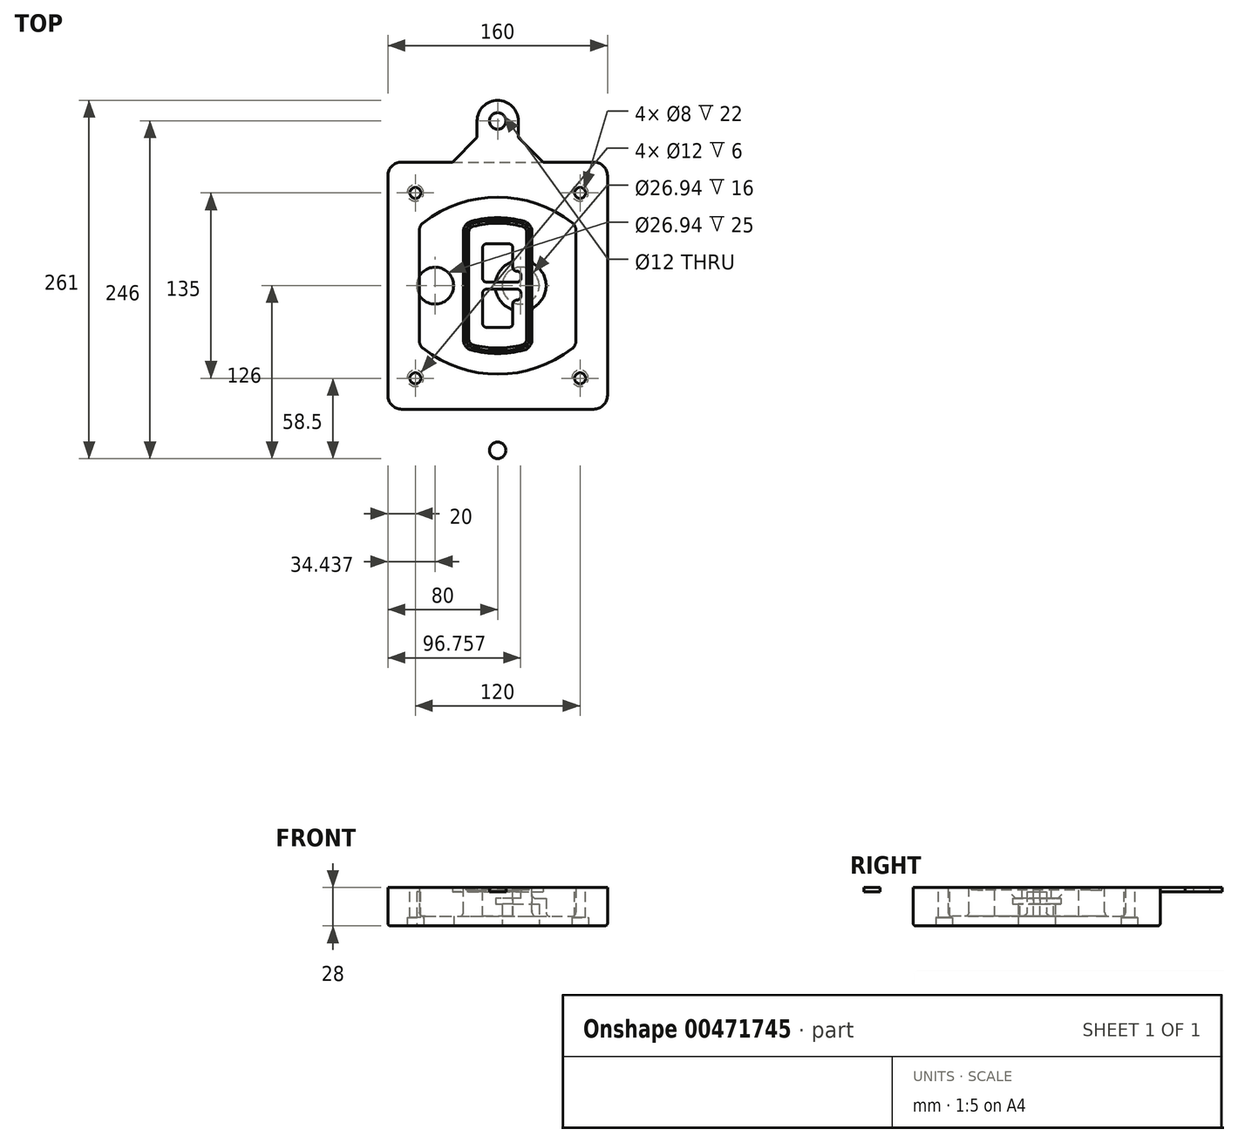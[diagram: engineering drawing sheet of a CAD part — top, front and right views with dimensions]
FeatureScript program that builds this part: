
annotation { "Feature Type Name" : "Feature", "Feature Type Description" : "" }
export const myFeature = defineFeature(function(context is Context, id is Id, definition is map)
    precondition{}
    {
        {
            var Q0;
            Q0=qCreatedBy(makeId("Top.planeOp"),FACE);
            var sketch = newSketch(context, id + "F0", { "sketchPlane" : qUnion([Q0])});
            skPoint(sketch, "E0.rect.middle", {"position": v(0, 0) * mm});
            skLineSegment(sketch, "E1.bottom", {"start": v(-70, -90) * mm, "end": v(70, -90) * mm});
            skLineSegment(sketch, "E1.top", {"start": v(-70, 90) * mm, "end": v(70, 90) * mm});
            skLineSegment(sketch, "E1.left", {"start": v(-80, -80) * mm, "end": v(-80, 80) * mm});
            skLineSegment(sketch, "E1.right", {"start": v(80, -80) * mm, "end": v(80, 80) * mm});
            skLineSegment(sketch, "E2", {"start": v(-80, 90) * mm, "end": v(80, -90) * mm, "construction": true});
            skLineSegment(sketch, "E3", {"start": v(80, 90) * mm, "end": v(-80, -90) * mm, "construction": true});
            skCircle(sketch, "E4", {"center": v(-60, 67.5) * mm, "radius": 4 * mm});
            skCircle(sketch, "E5", {"center": v(60, 67.5) * mm, "radius": 4 * mm});
            skCircle(sketch, "E6", {"center": v(60, -67.5) * mm, "radius": 4 * mm});
            skCircle(sketch, "E7", {"center": v(-60, -67.5) * mm, "radius": 4 * mm});
            skLineSegment(sketch, "E8", {"start": v(-60, 67.5) * mm, "end": v(60, 67.5) * mm, "construction": true});
            skLineSegment(sketch, "E9", {"start": v(60, 67.5) * mm, "end": v(60, -67.5) * mm, "construction": true});
            skLineSegment(sketch, "E10", {"start": v(60, -67.5) * mm, "end": v(-60, -67.5) * mm, "construction": true});
            skLineSegment(sketch, "E11", {"start": v(-60, -67.5) * mm, "end": v(-60, 67.5) * mm, "construction": true});
            skLineSegment(sketch, "E12", {"start": v(-60, 40.3) * mm, "end": v(-60, -40.3) * mm});
            skLineSegment(sketch, "E13", {"start": v(60, 40.3) * mm, "end": v(60, -40.3) * mm});
            skArc(sketch, "E14", {"start": v(56.15, 48.18) * mm, "mid": v(0, 67.5) * mm, "end": v(-56.15, 48.18) * mm});
            skArc(sketch, "E15", {"start": v(-56.15, -48.18) * mm, "mid": v(0, -67.5) * mm, "end": v(56.15, -48.18) * mm});
            skLineSegment(sketch, "E16", {"start": v(-60, 0) * mm, "end": v(60, 0) * mm, "construction": true});
            skPoint(sketch, "E17.visualSharp", {"position": v(-60, -45) * mm});
            skArc(sketch, "E17.filletArc", {"start": v(-60, -40.3) * mm, "mid": v(-58.99, -44.68) * mm, "end": v(-56.15, -48.18) * mm});
            skPoint(sketch, "E18.visualSharp", {"position": v(-60, 45) * mm});
            skArc(sketch, "E18.filletArc", {"start": v(-56.15, 48.18) * mm, "mid": v(-58.99, 44.68) * mm, "end": v(-60, 40.3) * mm});
            skPoint(sketch, "E19.visualSharp", {"position": v(60, 45) * mm});
            skArc(sketch, "E19.filletArc", {"start": v(60, 40.3) * mm, "mid": v(58.99, 44.68) * mm, "end": v(56.15, 48.18) * mm});
            skPoint(sketch, "E20.visualSharp", {"position": v(60, -45) * mm});
            skArc(sketch, "E20.filletArc", {"start": v(56.15, -48.18) * mm, "mid": v(58.99, -44.68) * mm, "end": v(60, -40.3) * mm});
            skPoint(sketch, "E21.visualSharp", {"position": v(-80, 90) * mm});
            skArc(sketch, "E21.filletArc", {"start": v(-70, 90) * mm, "mid": v(-77.07, 87.07) * mm, "end": v(-80, 80) * mm});
            skPoint(sketch, "E22.visualSharp", {"position": v(80, 90) * mm});
            skArc(sketch, "E22.filletArc", {"start": v(80, 80) * mm, "mid": v(77.07, 87.07) * mm, "end": v(70, 90) * mm});
            skPoint(sketch, "E23.visualSharp", {"position": v(80, -90) * mm});
            skArc(sketch, "E23.filletArc", {"start": v(70, -90) * mm, "mid": v(77.07, -87.07) * mm, "end": v(80, -80) * mm});
            skPoint(sketch, "E24.visualSharp", {"position": v(-80, -90) * mm});
            skArc(sketch, "E24.filletArc", {"start": v(-80, -80) * mm, "mid": v(-77.07, -87.07) * mm, "end": v(-70, -90) * mm});
            skArc(sketch, "E25.0", {"start": v(57, 40.3) * mm, "mid": v(56.3, 43.36) * mm, "end": v(54.3, 45.81) * mm});
            skLineSegment(sketch, "E25.1", {"start": v(57, 40.3) * mm, "end": v(57, -40.3) * mm});
            skArc(sketch, "E25.2", {"start": v(54.3, -45.81) * mm, "mid": v(56.3, -43.36) * mm, "end": v(57, -40.3) * mm});
            skArc(sketch, "E25.3", {"start": v(-54.3, -45.81) * mm, "mid": v(0, -64.5) * mm, "end": v(54.3, -45.81) * mm});
            skArc(sketch, "E25.4", {"start": v(-57, -40.3) * mm, "mid": v(-56.3, -43.36) * mm, "end": v(-54.3, -45.81) * mm});
            skArc(sketch, "E25.5", {"start": v(54.3, 45.81) * mm, "mid": v(0, 64.5) * mm, "end": v(-54.3, 45.81) * mm});
            skLineSegment(sketch, "E25.6", {"start": v(-57, 40.3) * mm, "end": v(-57, -40.3) * mm});
            skArc(sketch, "E25.7", {"start": v(-54.3, 45.81) * mm, "mid": v(-56.3, 43.36) * mm, "end": v(-57, 40.3) * mm});
            skArc(sketch, "E26.0", {"start": v(-58.62, 51.33) * mm, "mid": v(-62.58, 46.43) * mm, "end": v(-64, 40.3) * mm});
            skArc(sketch, "E26.1", {"start": v(58.62, 51.33) * mm, "mid": v(0, 71.5) * mm, "end": v(-58.62, 51.33) * mm});
            skArc(sketch, "E26.2", {"start": v(64, 40.3) * mm, "mid": v(62.58, 46.43) * mm, "end": v(58.62, 51.33) * mm});
            skLineSegment(sketch, "E26.3", {"start": v(64, 40.3) * mm, "end": v(64, -40.3) * mm});
            skArc(sketch, "E26.4", {"start": v(58.62, -51.33) * mm, "mid": v(62.58, -46.43) * mm, "end": v(64, -40.3) * mm});
            skLineSegment(sketch, "E26.5", {"start": v(-64, 40.3) * mm, "end": v(-64, -40.3) * mm});
            skArc(sketch, "E26.6", {"start": v(-58.62, -51.33) * mm, "mid": v(0, -71.5) * mm, "end": v(58.62, -51.33) * mm});
            skArc(sketch, "E26.7", {"start": v(-64, -40.3) * mm, "mid": v(-62.58, -46.43) * mm, "end": v(-58.62, -51.33) * mm});
            skSolve(sketch);
        }
        {
            var Q0;
            Q0=makeQuery(id+"F0.imprint","IMPRINT",FACE,{"disambiguationData":[TD([[makeQuery(id+"F0.imprint","IMPRINT",EDGE,{"derivedFrom":sQuery(id+"F0.wireOp",EDGE,"E1.bottom")}),1.0]])]});
            var Q1;
            Q1=makeQuery(id+"F0.imprint","IMPRINT",FACE,{"disambiguationData":[TD([[makeQuery(id+"F0.imprint","IMPRINT",EDGE,{"derivedFrom":sQuery(id+"F0.wireOp",EDGE,"E12")}),1.0]])]});
            var Q2;
            Q2=makeQuery(id+"F0.imprint","IMPRINT",FACE,{"disambiguationData":[TD([[makeQuery(id+"F0.imprint","IMPRINT",EDGE,{"derivedFrom":sQuery(id+"F0.wireOp",EDGE,"E25.0")}),1.0]])]});
            var Q3;
            Q3=makeQuery(id+"F0.imprint","IMPRINT",FACE,{"disambiguationData":[TD([[makeQuery(id+"F0.imprint","IMPRINT",EDGE,{"derivedFrom":sQuery(id+"F0.wireOp",EDGE,"E12")}),-1.0]])]});
            extrude(context, id + "F1", {"entities" : qUnion([Q0, Q1, Q2, Q3]), "oppositeDirection" : true, "depth" : 25 * mm});
        }
        {
            var Q0;
            Q0=makeQuery(id+"F0.imprint","IMPRINT",FACE,{"disambiguationData":[TD([[makeQuery(id+"F0.imprint","IMPRINT",EDGE,{"derivedFrom":sQuery(id+"F0.wireOp",EDGE,"E12")}),1.0]])]});
            extrude(context, id + "F2", {"entities" : qUnion([Q0]), "operationType" : NewBodyOperationType.ADD, "depth" : 3 * mm});
        }
        {
            var Q0;
            Q0=makeQuery(id+"F0.imprint","IMPRINT",FACE,{"disambiguationData":[TD([[makeQuery(id+"F0.imprint","IMPRINT",EDGE,{"derivedFrom":sQuery(id+"F0.wireOp",EDGE,"E25.0")}),1.0]])]});
            extrude(context, id + "F3", {"entities" : qUnion([Q0]), "operationType" : NewBodyOperationType.REMOVE, "oppositeDirection" : true, "depth" : 18 * mm});
        }
        {
            var Q0;
            Q0=makeQuery(id+"F2.opExtrude","CAP_FACE",FACE,{"disambiguationData":[OSD([sQuery(id+"F0.wireOp",EDGE,"E12"),sQuery(id+"F0.wireOp",EDGE,"E13"),sQuery(id+"F0.wireOp",EDGE,"E14"),sQuery(id+"F0.wireOp",EDGE,"E15"),sQuery(id+"F0.wireOp",EDGE,"E17.filletArc"),sQuery(id+"F0.wireOp",EDGE,"E18.filletArc"),sQuery(id+"F0.wireOp",EDGE,"E19.filletArc"),sQuery(id+"F0.wireOp",EDGE,"E20.filletArc"),sQuery(id+"F0.wireOp",EDGE,"E25.0"),sQuery(id+"F0.wireOp",EDGE,"E25.1"),sQuery(id+"F0.wireOp",EDGE,"E25.2"),sQuery(id+"F0.wireOp",EDGE,"E25.3"),sQuery(id+"F0.wireOp",EDGE,"E25.4"),sQuery(id+"F0.wireOp",EDGE,"E25.5"),sQuery(id+"F0.wireOp",EDGE,"E25.6"),sQuery(id+"F0.wireOp",EDGE,"E25.7")])],"isStart":false});
            var sketch = newSketch(context, id + "F4", { "sketchPlane" : qUnion([Q0])});
            skArc(sketch, "E27.0", {"start": v(-19.08, -46.97) * mm, "mid": v(0, -49.5) * mm, "end": v(19.08, -46.97) * mm});
            skArc(sketch, "E28.0", {"start": v(19.08, 46.97) * mm, "mid": v(0, 49.5) * mm, "end": v(-19.08, 46.97) * mm});
            skLineSegment(sketch, "E29", {"start": v(-25, 39.25) * mm, "end": v(-25, -39.25) * mm});
            skLineSegment(sketch, "E30", {"start": v(25, 39.25) * mm, "end": v(25, -39.25) * mm});
            skLineSegment(sketch, "E31", {"start": v(-25, 45.1) * mm, "end": v(25, 45.1) * mm, "construction": true});
            skLineSegment(sketch, "E32", {"start": v(-25, -45.1) * mm, "end": v(25, -45.1) * mm, "construction": true});
            skPoint(sketch, "E33.visualSharp", {"position": v(-25, 45.1) * mm});
            skArc(sketch, "E33.filletArc", {"start": v(-19.08, 46.97) * mm, "mid": v(-23.35, 44.11) * mm, "end": v(-25, 39.25) * mm});
            skPoint(sketch, "E34.visualSharp", {"position": v(25, 45.1) * mm});
            skArc(sketch, "E34.filletArc", {"start": v(25, 39.25) * mm, "mid": v(23.35, 44.11) * mm, "end": v(19.08, 46.97) * mm});
            skPoint(sketch, "E35.visualSharp", {"position": v(25, -45.1) * mm});
            skArc(sketch, "E35.filletArc", {"start": v(19.08, -46.97) * mm, "mid": v(23.35, -44.11) * mm, "end": v(25, -39.25) * mm});
            skPoint(sketch, "E36.visualSharp", {"position": v(-25, -45.1) * mm});
            skArc(sketch, "E36.filletArc", {"start": v(-25, -39.25) * mm, "mid": v(-23.35, -44.11) * mm, "end": v(-19.08, -46.97) * mm});
            skArc(sketch, "E37.0", {"start": v(54.3, 45.81) * mm, "mid": v(0, 64.5) * mm, "end": v(-54.3, 45.81) * mm});
            skArc(sketch, "E37.1", {"start": v(-54.3, 45.81) * mm, "mid": v(-56.3, 43.36) * mm, "end": v(-57, 40.3) * mm});
            skLineSegment(sketch, "E37.2", {"start": v(-57, 40.3) * mm, "end": v(-57, -40.3) * mm});
            skArc(sketch, "E37.3", {"start": v(-57, -40.3) * mm, "mid": v(-56.3, -43.36) * mm, "end": v(-54.3, -45.81) * mm});
            skArc(sketch, "E37.4", {"start": v(-54.3, -45.81) * mm, "mid": v(0, -64.5) * mm, "end": v(54.3, -45.81) * mm});
            skArc(sketch, "E37.5", {"start": v(54.3, -45.81) * mm, "mid": v(56.3, -43.36) * mm, "end": v(57, -40.3) * mm});
            skLineSegment(sketch, "E37.6", {"start": v(57, 40.3) * mm, "end": v(57, -40.3) * mm});
            skArc(sketch, "E37.7", {"start": v(57, 40.3) * mm, "mid": v(56.3, 43.36) * mm, "end": v(54.3, 45.81) * mm});
            skLineSegment(sketch, "E38.0", {"start": v(23, 39.25) * mm, "end": v(23, -39.25) * mm});
            skArc(sketch, "E38.1", {"start": v(18.56, -45.04) * mm, "mid": v(21.76, -42.9) * mm, "end": v(23, -39.25) * mm});
            skArc(sketch, "E38.2", {"start": v(-18.56, -45.04) * mm, "mid": v(0, -47.5) * mm, "end": v(18.56, -45.04) * mm});
            skArc(sketch, "E38.3", {"start": v(-23, -39.25) * mm, "mid": v(-21.76, -42.9) * mm, "end": v(-18.56, -45.04) * mm});
            skLineSegment(sketch, "E38.4", {"start": v(-23, 39.25) * mm, "end": v(-23, -39.25) * mm});
            skArc(sketch, "E38.5", {"start": v(23, 39.25) * mm, "mid": v(21.76, 42.9) * mm, "end": v(18.56, 45.04) * mm});
            skArc(sketch, "E38.6", {"start": v(-18.56, 45.04) * mm, "mid": v(-21.76, 42.9) * mm, "end": v(-23, 39.25) * mm});
            skArc(sketch, "E38.7", {"start": v(18.56, 45.04) * mm, "mid": v(0, 47.5) * mm, "end": v(-18.56, 45.04) * mm});
            skArc(sketch, "E39.0", {"start": v(21, 39.25) * mm, "mid": v(20.18, 41.68) * mm, "end": v(18.04, 43.1) * mm});
            skLineSegment(sketch, "E39.1", {"start": v(21, 39.25) * mm, "end": v(21, -39.25) * mm});
            skArc(sketch, "E39.2", {"start": v(18.04, -43.1) * mm, "mid": v(20.18, -41.68) * mm, "end": v(21, -39.25) * mm});
            skArc(sketch, "E39.3", {"start": v(-18.04, -43.1) * mm, "mid": v(0, -45.5) * mm, "end": v(18.04, -43.1) * mm});
            skArc(sketch, "E39.4", {"start": v(-21, -39.25) * mm, "mid": v(-20.18, -41.68) * mm, "end": v(-18.04, -43.1) * mm});
            skArc(sketch, "E39.5", {"start": v(18.04, 43.1) * mm, "mid": v(0, 45.5) * mm, "end": v(-18.04, 43.1) * mm});
            skLineSegment(sketch, "E39.6", {"start": v(-21, 39.25) * mm, "end": v(-21, -39.25) * mm});
            skArc(sketch, "E39.7", {"start": v(-18.04, 43.1) * mm, "mid": v(-20.18, 41.68) * mm, "end": v(-21, 39.25) * mm});
            skLineSegment(sketch, "E40", {"start": v(-25, 0) * mm, "end": v(25, 0) * mm, "construction": true});
            skLineSegment(sketch, "E41", {"start": v(-11, 5.5) * mm, "end": v(-11, 27.5) * mm});
            skLineSegment(sketch, "E42", {"start": v(-8, 30.5) * mm, "end": v(8, 30.5) * mm});
            skLineSegment(sketch, "E43", {"start": v(11, 27.5) * mm, "end": v(11, 13.5) * mm});
            skLineSegment(sketch, "E44", {"start": v(14, 10.5) * mm, "end": v(14, 10.5) * mm});
            skLineSegment(sketch, "E45", {"start": v(17, 7.5) * mm, "end": v(17, 5.5) * mm});
            skLineSegment(sketch, "E46", {"start": v(14, 2.5) * mm, "end": v(-8, 2.5) * mm});
            skPoint(sketch, "E47.visualSharp", {"position": v(-11, 30.5) * mm});
            skArc(sketch, "E47.filletArc", {"start": v(-8, 30.5) * mm, "mid": v(-10.12, 29.62) * mm, "end": v(-11, 27.5) * mm});
            skPoint(sketch, "E48.visualSharp", {"position": v(11, 30.5) * mm});
            skArc(sketch, "E48.filletArc", {"start": v(11, 27.5) * mm, "mid": v(10.12, 29.62) * mm, "end": v(8, 30.5) * mm});
            skPoint(sketch, "E49.visualSharp", {"position": v(11, 10.5) * mm});
            skArc(sketch, "E49.filletArc", {"start": v(11, 13.5) * mm, "mid": v(11.88, 11.38) * mm, "end": v(14, 10.5) * mm});
            skPoint(sketch, "E50.visualSharp", {"position": v(17, 10.5) * mm});
            skArc(sketch, "E50.filletArc", {"start": v(17, 7.5) * mm, "mid": v(16.12, 9.62) * mm, "end": v(14, 10.5) * mm});
            skPoint(sketch, "E51.visualSharp", {"position": v(17, 2.5) * mm});
            skArc(sketch, "E51.filletArc", {"start": v(14, 2.5) * mm, "mid": v(16.12, 3.38) * mm, "end": v(17, 5.5) * mm});
            skPoint(sketch, "E52.visualSharp", {"position": v(-11, 2.5) * mm});
            skArc(sketch, "E52.filletArc", {"start": v(-11, 5.5) * mm, "mid": v(-10.12, 3.38) * mm, "end": v(-8, 2.5) * mm});
            skLineSegment(sketch, "E53.0.MirrorCS", {"start": v(14, -2.5) * mm, "end": v(-8, -2.5) * mm});
            skArc(sketch, "E54.0.MirrorCS", {"start": v(-11, -5.5) * mm, "mid": v(-10.12, -3.38) * mm, "end": v(-8, -2.5) * mm});
            skLineSegment(sketch, "E55.0.MirrorCS", {"start": v(-11, -5.5) * mm, "end": v(-11, -27.5) * mm});
            skArc(sketch, "E56.0.MirrorCS", {"start": v(-8, -30.5) * mm, "mid": v(-10.12, -29.62) * mm, "end": v(-11, -27.5) * mm});
            skLineSegment(sketch, "E57.0.MirrorCS", {"start": v(-8, -30.5) * mm, "end": v(8, -30.5) * mm});
            skArc(sketch, "E58.0.MirrorCS", {"start": v(11, -27.5) * mm, "mid": v(10.12, -29.62) * mm, "end": v(8, -30.5) * mm});
            skLineSegment(sketch, "E59.0.MirrorCS", {"start": v(11, -27.5) * mm, "end": v(11, -13.5) * mm});
            skArc(sketch, "E60.0.MirrorCS", {"start": v(11, -13.5) * mm, "mid": v(11.88, -11.38) * mm, "end": v(14, -10.5) * mm});
            skArc(sketch, "E61.0.MirrorCS", {"start": v(17, -7.5) * mm, "mid": v(16.12, -9.62) * mm, "end": v(14, -10.5) * mm});
            skLineSegment(sketch, "E62.0.MirrorCS", {"start": v(17, -7.5) * mm, "end": v(17, -5.5) * mm});
            skArc(sketch, "E63.0.MirrorCS", {"start": v(14, -2.5) * mm, "mid": v(16.12, -3.38) * mm, "end": v(17, -5.5) * mm});
            skSolve(sketch);
        }
        {
            var Q0;
            Q0=makeQuery(id+"F4.imprint","IMPRINT",FACE,{"disambiguationData":[TD([[makeQuery(id+"F4.imprint","IMPRINT",EDGE,{"derivedFrom":sQuery(id+"F4.wireOp",EDGE,"E27.0")}),1.0]])]});
            var Q1;
            Q1=makeQuery(id+"F4.imprint","IMPRINT",FACE,{"disambiguationData":[TD([[makeQuery(id+"F4.imprint","IMPRINT",EDGE,{"derivedFrom":sQuery(id+"F4.wireOp",EDGE,"E38.0")}),-1.0]])]});
            var Q2;
            Q2=makeQuery(id+"F4.imprint","IMPRINT",FACE,{"disambiguationData":[TD([[makeQuery(id+"F4.imprint","IMPRINT",EDGE,{"derivedFrom":sQuery(id+"F4.wireOp",EDGE,"E39.0")}),1.0]])]});
            extrude(context, id + "F5", {"entities" : qUnion([Q0, Q1, Q2]), "operationType" : NewBodyOperationType.ADD, "endBound" : BoundingType.UP_TO_NEXT, "oppositeDirection" : true, "depth" : 25 * mm});
        }
        {
            var Q0;
            Q0=makeQuery(id+"F4.imprint","IMPRINT",FACE,{"disambiguationData":[TD([[makeQuery(id+"F4.imprint","IMPRINT",EDGE,{"derivedFrom":sQuery(id+"F4.wireOp",EDGE,"E38.0")}),-1.0]])]});
            extrude(context, id + "F6", {"entities" : qUnion([Q0]), "operationType" : NewBodyOperationType.REMOVE, "oppositeDirection" : true, "depth" : 2 * mm});
        }
        {
            var Q0;
            Q0=makeQuery(id+"F1.opExtrude","CAP_FACE",FACE,{"disambiguationData":[OSD([sQuery(id+"F0.wireOp",EDGE,"E1.bottom"),sQuery(id+"F0.wireOp",EDGE,"E1.top"),sQuery(id+"F0.wireOp",EDGE,"E1.left"),sQuery(id+"F0.wireOp",EDGE,"E1.right"),sQuery(id+"F0.wireOp",EDGE,"E4"),sQuery(id+"F0.wireOp",EDGE,"E5"),sQuery(id+"F0.wireOp",EDGE,"E6"),sQuery(id+"F0.wireOp",EDGE,"E7"),sQuery(id+"F0.wireOp",EDGE,"E21.filletArc"),sQuery(id+"F0.wireOp",EDGE,"E22.filletArc"),sQuery(id+"F0.wireOp",EDGE,"E23.filletArc"),sQuery(id+"F0.wireOp",EDGE,"E24.filletArc")])],"isStart":false});
            var sketch = newSketch(context, id + "F7", { "sketchPlane" : qUnion([Q0])});
            skCircle(sketch, "E64", {"center": v(16.76, 0) * mm, "radius": 13.47 * mm});
            skCircle(sketch, "E65", {"center": v(-45.56, 0) * mm, "radius": 13.47 * mm});
            skLineSegment(sketch, "E66", {"start": v(80, 0) * mm, "end": v(-80, 0) * mm});
            skCircle(sketch, "E67", {"center": v(16.76, 0) * mm, "radius": 18.47 * mm});
            skCircle(sketch, "E68", {"center": v(60, -67.5) * mm, "radius": 6 * mm});
            skCircle(sketch, "E69", {"center": v(-60, -67.5) * mm, "radius": 6 * mm});
            skCircle(sketch, "E70", {"center": v(-60, 67.5) * mm, "radius": 6 * mm});
            skCircle(sketch, "E71", {"center": v(60, 67.5) * mm, "radius": 6 * mm});
            skSolve(sketch);
        }
        {
            var Q0;
            {var subQ1=sQuery(id+"F7.wireOp",EDGE,"E66");var subQ4=sQuery(id+"F7.wireOp",EDGE,"E64");var subQ6=makeQuery(id+"F7.imprint","INTERSECT",VERTEX,{"disambiguationData":[OD(0.0)],"derivedFrom":[subQ4,subQ1]});Q0=makeQuery(id+"F7.imprint","IMPRINT",FACE,{"disambiguationData":[TD([[makeQuery(id+"F7.imprint","IMPRINT",EDGE,{"disambiguationData":[TD([[subQ6,-1.0]])],"derivedFrom":subQ4}),-1.0]])]});}
            var Q1;
            {var subQ0=sQuery(id+"F7.wireOp",EDGE,"E66");var subQ1=sQuery(id+"F7.wireOp",EDGE,"E64");var subQ3=makeQuery(id+"F7.imprint","INTERSECT",VERTEX,{"disambiguationData":[OD(0.0)],"derivedFrom":[subQ1,subQ0]});Q1=makeQuery(id+"F7.imprint","IMPRINT",FACE,{"disambiguationData":[TD([[makeQuery(id+"F7.imprint","IMPRINT",EDGE,{"disambiguationData":[TD([[subQ3,-1.0]])],"derivedFrom":subQ1}),1.0]])]});}
            var Q2;
            {var subQ0=sQuery(id+"F7.wireOp",EDGE,"E66");var subQ1=sQuery(id+"F7.wireOp",EDGE,"E64");var subQ3=makeQuery(id+"F7.imprint","INTERSECT",VERTEX,{"disambiguationData":[OD(0.0)],"derivedFrom":[subQ1,subQ0]});Q2=makeQuery(id+"F7.imprint","IMPRINT",FACE,{"disambiguationData":[TD([[makeQuery(id+"F7.imprint","IMPRINT",EDGE,{"disambiguationData":[TD([[subQ3,1.0]])],"derivedFrom":subQ1}),1.0]])]});}
            var Q3;
            {var subQ1=sQuery(id+"F7.wireOp",EDGE,"E66");var subQ4=sQuery(id+"F7.wireOp",EDGE,"E64");var subQ6=makeQuery(id+"F7.imprint","INTERSECT",VERTEX,{"disambiguationData":[OD(0.0)],"derivedFrom":[subQ4,subQ1]});Q3=makeQuery(id+"F7.imprint","IMPRINT",FACE,{"disambiguationData":[TD([[makeQuery(id+"F7.imprint","IMPRINT",EDGE,{"disambiguationData":[TD([[subQ6,1.0]])],"derivedFrom":subQ4}),-1.0]])]});}
            extrude(context, id + "F8", {"entities" : qUnion([Q0, Q1, Q2, Q3]), "operationType" : NewBodyOperationType.ADD, "oppositeDirection" : true, "depth" : 20 * mm});
        }
        {
            var Q0;
            {var subQ0=sQuery(id+"F7.wireOp",EDGE,"E66");var subQ1=sQuery(id+"F7.wireOp",EDGE,"E64");var subQ3=makeQuery(id+"F7.imprint","INTERSECT",VERTEX,{"disambiguationData":[OD(0.0)],"derivedFrom":[subQ1,subQ0]});Q0=makeQuery(id+"F7.imprint","IMPRINT",FACE,{"disambiguationData":[TD([[makeQuery(id+"F7.imprint","IMPRINT",EDGE,{"disambiguationData":[TD([[subQ3,-1.0]])],"derivedFrom":subQ1}),1.0]])]});}
            var Q1;
            {var subQ0=sQuery(id+"F7.wireOp",EDGE,"E66");var subQ1=sQuery(id+"F7.wireOp",EDGE,"E64");var subQ3=makeQuery(id+"F7.imprint","INTERSECT",VERTEX,{"disambiguationData":[OD(0.0)],"derivedFrom":[subQ1,subQ0]});Q1=makeQuery(id+"F7.imprint","IMPRINT",FACE,{"disambiguationData":[TD([[makeQuery(id+"F7.imprint","IMPRINT",EDGE,{"disambiguationData":[TD([[subQ3,1.0]])],"derivedFrom":subQ1}),1.0]])]});}
            extrude(context, id + "F9", {"entities" : qUnion([Q0, Q1]), "operationType" : NewBodyOperationType.REMOVE, "oppositeDirection" : true, "depth" : 16 * mm});
        }
        {
            var Q0;
            {var subQ0=sQuery(id+"F7.wireOp",EDGE,"E66");var subQ1=sQuery(id+"F7.wireOp",EDGE,"E65");var subQ3=makeQuery(id+"F7.imprint","INTERSECT",VERTEX,{"disambiguationData":[OD(0.0)],"derivedFrom":[subQ1,subQ0]});Q0=makeQuery(id+"F7.imprint","IMPRINT",FACE,{"disambiguationData":[TD([[makeQuery(id+"F7.imprint","IMPRINT",EDGE,{"disambiguationData":[TD([[subQ3,-1.0]])],"derivedFrom":subQ1}),1.0]])]});}
            var Q1;
            {var subQ0=sQuery(id+"F7.wireOp",EDGE,"E66");var subQ1=sQuery(id+"F7.wireOp",EDGE,"E65");var subQ3=makeQuery(id+"F7.imprint","INTERSECT",VERTEX,{"disambiguationData":[OD(0.0)],"derivedFrom":[subQ1,subQ0]});Q1=makeQuery(id+"F7.imprint","IMPRINT",FACE,{"disambiguationData":[TD([[makeQuery(id+"F7.imprint","IMPRINT",EDGE,{"disambiguationData":[TD([[subQ3,1.0]])],"derivedFrom":subQ1}),1.0]])]});}
            extrude(context, id + "F10", {"entities" : qUnion([Q0, Q1]), "operationType" : NewBodyOperationType.REMOVE, "oppositeDirection" : true, "depth" : 25 * mm});
        }
        {
            var Q0;
            Q0=makeQuery(id+"F7.imprint","IMPRINT",FACE,{"disambiguationData":[TD([[makeQuery(id+"F7.imprint","IMPRINT",EDGE,{"derivedFrom":sQuery(id+"F7.wireOp",EDGE,"E68")}),1.0]])]});
            var Q1;
            Q1=makeQuery(id+"F7.imprint","IMPRINT",FACE,{"disambiguationData":[TD([[makeQuery(id+"F7.imprint","IMPRINT",EDGE,{"derivedFrom":makeQuery(id+"F1.opExtrude","CAP_EDGE",EDGE,{"disambiguationData":[OSD([sQuery(id+"F0.wireOp",EDGE,"E5")])],"isStart":false})}),-1.0]])]});
            var Q2;
            Q2=makeQuery(id+"F7.imprint","IMPRINT",FACE,{"disambiguationData":[TD([[makeQuery(id+"F7.imprint","IMPRINT",EDGE,{"derivedFrom":sQuery(id+"F7.wireOp",EDGE,"E69")}),1.0]])]});
            var Q3;
            Q3=makeQuery(id+"F7.imprint","IMPRINT",FACE,{"disambiguationData":[TD([[makeQuery(id+"F7.imprint","IMPRINT",EDGE,{"derivedFrom":makeQuery(id+"F1.opExtrude","CAP_EDGE",EDGE,{"disambiguationData":[OSD([sQuery(id+"F0.wireOp",EDGE,"E4")])],"isStart":false})}),-1.0]])]});
            var Q4;
            Q4=makeQuery(id+"F7.imprint","IMPRINT",FACE,{"disambiguationData":[TD([[makeQuery(id+"F7.imprint","IMPRINT",EDGE,{"derivedFrom":sQuery(id+"F7.wireOp",EDGE,"E70")}),1.0]])]});
            var Q5;
            Q5=makeQuery(id+"F7.imprint","IMPRINT",FACE,{"disambiguationData":[TD([[makeQuery(id+"F7.imprint","IMPRINT",EDGE,{"derivedFrom":makeQuery(id+"F1.opExtrude","CAP_EDGE",EDGE,{"disambiguationData":[OSD([sQuery(id+"F0.wireOp",EDGE,"E7")])],"isStart":false})}),-1.0]])]});
            var Q6;
            Q6=makeQuery(id+"F7.imprint","IMPRINT",FACE,{"disambiguationData":[TD([[makeQuery(id+"F7.imprint","IMPRINT",EDGE,{"derivedFrom":sQuery(id+"F7.wireOp",EDGE,"E71")}),1.0]])]});
            var Q7;
            Q7=makeQuery(id+"F7.imprint","IMPRINT",FACE,{"disambiguationData":[TD([[makeQuery(id+"F7.imprint","IMPRINT",EDGE,{"derivedFrom":makeQuery(id+"F1.opExtrude","CAP_EDGE",EDGE,{"disambiguationData":[OSD([sQuery(id+"F0.wireOp",EDGE,"E6")])],"isStart":false})}),-1.0]])]});
            extrude(context, id + "F11", {"entities" : qUnion([Q0, Q1, Q2, Q3, Q4, Q5, Q6, Q7]), "operationType" : NewBodyOperationType.REMOVE, "oppositeDirection" : true, "depth" : 6 * mm});
        }
        {
            var Q0;
            Q0=makeQuery(id+"F9.boolean.opBoolean","COPY",FACE,{"derivedFrom":makeQuery(id+"F9.opExtrude","CAP_FACE",FACE,{"disambiguationData":[OSD([sQuery(id+"F7.wireOp",EDGE,"E64")])],"isStart":false})});
            var sketch = newSketch(context, id + "F12", { "sketchPlane" : qUnion([Q0])});
            skArc(sketch, "E72.0", {"start": v(11, 17.55) * mm, "mid": v(2.57, 11.82) * mm, "end": v(-1.54, 2.5) * mm});
            skArc(sketch, "E72.1", {"start": v(-1.54, -2.5) * mm, "mid": v(2.57, -11.82) * mm, "end": v(11, -17.55) * mm});
            skLineSegment(sketch, "E73", {"start": v(-1.54, -2.5) * mm, "end": v(14, -2.5) * mm});
            skLineSegment(sketch, "E74.0", {"start": v(14, 2.5) * mm, "end": v(-1.54, 2.5) * mm});
            skArc(sketch, "E74.1", {"start": v(14, 2.5) * mm, "mid": v(16.12, 3.38) * mm, "end": v(17, 5.5) * mm});
            skLineSegment(sketch, "E74.2", {"start": v(17, 7.5) * mm, "end": v(17, 5.5) * mm});
            skArc(sketch, "E74.3", {"start": v(17, 7.5) * mm, "mid": v(16.12, 9.62) * mm, "end": v(14, 10.5) * mm});
            skArc(sketch, "E74.4", {"start": v(11, 13.5) * mm, "mid": v(11.88, 11.38) * mm, "end": v(14, 10.5) * mm});
            skLineSegment(sketch, "E74.5", {"start": v(11, 17.55) * mm, "end": v(11, 13.5) * mm});
            skLineSegment(sketch, "E74.7", {"start": v(14, -2.5) * mm, "end": v(-1.54, -2.5) * mm});
            skArc(sketch, "E74.8", {"start": v(14, -2.5) * mm, "mid": v(16.12, -3.38) * mm, "end": v(17, -5.5) * mm});
            skLineSegment(sketch, "E74.9", {"start": v(17, -7.5) * mm, "end": v(17, -5.5) * mm});
            skArc(sketch, "E74.10", {"start": v(17, -7.5) * mm, "mid": v(16.12, -9.62) * mm, "end": v(14, -10.5) * mm});
            skArc(sketch, "E74.11", {"start": v(11, -13.5) * mm, "mid": v(11.88, -11.38) * mm, "end": v(14, -10.5) * mm});
            skLineSegment(sketch, "E74.12", {"start": v(11, -17.55) * mm, "end": v(11, -13.5) * mm});
            skPoint(sketch, "E75.orphan", {"position": v(11, -27.5) * mm});
            skPoint(sketch, "E76.orphan", {"position": v(-8, -2.5) * mm});
            skPoint(sketch, "E77.orphan", {"position": v(-8, 2.5) * mm});
            skPoint(sketch, "E78.orphan", {"position": v(11, 27.5) * mm});
            skSolve(sketch);
        }
        {
            var Q0;
            {var subQ7=sQuery(id+"F12.wireOp",EDGE,"E72.0");var subQ14=sQuery(id+"F12.wireOp",EDGE,"E72.1");var subQ16=sQuery(id+"F12.wireOp",EDGE,"E74.1");var subQ18=sQuery(id+"F12.wireOp",EDGE,"E74.8");Q0=qUnion([makeQuery(id+"F12.imprint","IMPRINT",FACE,{"disambiguationData":[TD([[makeQuery(id+"F12.imprint","IMPRINT",EDGE,{"derivedFrom":subQ7}),1.0]])]}),makeQuery(id+"F12.imprint","IMPRINT",FACE,{"disambiguationData":[TD([[makeQuery(id+"F12.imprint","IMPRINT",EDGE,{"derivedFrom":subQ14}),1.0]])]}),makeQuery(id+"F12.imprint","IMPRINT",FACE,{"disambiguationData":[TD([[makeQuery(id+"F12.imprint","IMPRINT",EDGE,{"derivedFrom":subQ16}),1.0]])]}),makeQuery(id+"F12.imprint","IMPRINT",FACE,{"disambiguationData":[TD([[makeQuery(id+"F12.imprint","IMPRINT",EDGE,{"derivedFrom":subQ18}),-1.0]])]})]);}
            var Q1;
            Q1=makeQuery(id+"F5.boolean.opBoolean","SPLIT",FACE,{"disambiguationData":[TD([makeQuery(id+"F5.opExtrude","SWEPT_FACE",FACE,{"disambiguationData":[OSD([sQuery(id+"F4.wireOp",EDGE,"E41")])]})])],"derivedFrom":makeQuery(id+"F3.boolean.opBoolean","COPY",FACE,{"derivedFrom":makeQuery(id+"F3.opExtrude","CAP_FACE",FACE,{"disambiguationData":[OSD([sQuery(id+"F0.wireOp",EDGE,"E25.0"),sQuery(id+"F0.wireOp",EDGE,"E25.1"),sQuery(id+"F0.wireOp",EDGE,"E25.2"),sQuery(id+"F0.wireOp",EDGE,"E25.3"),sQuery(id+"F0.wireOp",EDGE,"E25.4"),sQuery(id+"F0.wireOp",EDGE,"E25.5"),sQuery(id+"F0.wireOp",EDGE,"E25.6"),sQuery(id+"F0.wireOp",EDGE,"E25.7")])],"isStart":false})})});
            extrude(context, id + "F13", {"entities" : qUnion([Q0]), "operationType" : NewBodyOperationType.REMOVE, "endBound" : BoundingType.UP_TO_SURFACE, "endBoundEntityFace" : qUnion([Q1]), "depth" : 25 * mm});
        }
        {
            var Q0;
            Q0=makeQuery(id+"F3.boolean.opBoolean","COPY",EDGE,{"derivedFrom":makeQuery(id+"F3.opExtrude","CAP_EDGE",EDGE,{"disambiguationData":[OSD([sQuery(id+"F0.wireOp",EDGE,"E25.6")])],"isStart":false})});
            var Q1;
            Q1=makeQuery(id+"F8.boolean.opBoolean","INTERSECT",EDGE,{"derivedFrom":[makeQuery(id+"F5.opExtrude","SWEPT_FACE",FACE,{"disambiguationData":[OSD([sQuery(id+"F4.wireOp",EDGE,"E30")])]}),makeQuery(id+"F8.opExtrude","CAP_FACE",FACE,{"disambiguationData":[OSD([sQuery(id+"F7.wireOp",EDGE,"E67")])],"isStart":false})]});
            var Q2;
            Q2=makeQuery(id+"F8.boolean.opBoolean","INTERSECT",EDGE,{"disambiguationData":[OD(1.0)],"derivedFrom":[makeQuery(id+"F5.opExtrude","SWEPT_FACE",FACE,{"disambiguationData":[OSD([sQuery(id+"F4.wireOp",EDGE,"E30")])]}),makeQuery(id+"F8.opExtrude","SWEPT_FACE",FACE,{"disambiguationData":[OSD([sQuery(id+"F7.wireOp",EDGE,"E67")])]})]});
            var Q3;
            {var subQ0=sQuery(id+"F4.wireOp",EDGE,"E30");Q3=makeQuery(id+"F8.boolean.opBoolean","SPLIT",EDGE,{"disambiguationData":[TD([makeQuery(id+"F5.opExtrude","SWEPT_FACE",FACE,{"disambiguationData":[OSD([sQuery(id+"F4.wireOp",EDGE,"E35.filletArc")])]})])],"derivedFrom":makeQuery(id+"F5.opExtrude","CAP_EDGE",EDGE,{"disambiguationData":[OSD([subQ0])],"isStart":false})});}
            var Q4;
            {var subQ0=sQuery(id+"F0.wireOp",EDGE,"E25.7");var subQ1=sQuery(id+"F0.wireOp",EDGE,"E25.1");var subQ2=sQuery(id+"F0.wireOp",EDGE,"E25.6");var subQ3=sQuery(id+"F0.wireOp",EDGE,"E25.5");var subQ4=sQuery(id+"F0.wireOp",EDGE,"E25.4");var subQ5=sQuery(id+"F0.wireOp",EDGE,"E25.0");var subQ6=sQuery(id+"F0.wireOp",EDGE,"E25.2");var subQ7=sQuery(id+"F0.wireOp",EDGE,"E25.3");Q4=makeQuery(id+"F8.boolean.opBoolean","INTERSECT",EDGE,{"derivedFrom":[makeQuery(id+"F5.boolean.opBoolean","SPLIT",FACE,{"disambiguationData":[TD([makeQuery(id+"F2.opExtrude","SWEPT_FACE",FACE,{"disambiguationData":[OSD([subQ5])]})])],"derivedFrom":makeQuery(id+"F3.boolean.opBoolean","COPY",FACE,{"derivedFrom":makeQuery(id+"F3.opExtrude","CAP_FACE",FACE,{"disambiguationData":[OSD([subQ5,subQ1,subQ6,subQ7,subQ4,subQ3,subQ2,subQ0])],"isStart":false})})}),makeQuery(id+"F8.opExtrude","SWEPT_FACE",FACE,{"disambiguationData":[OSD([sQuery(id+"F7.wireOp",EDGE,"E67")])]})]});}
            var Q5;
            Q5=makeQuery(id+"F8.boolean.opBoolean","INTERSECT",EDGE,{"disambiguationData":[OD(0.0)],"derivedFrom":[makeQuery(id+"F5.opExtrude","SWEPT_FACE",FACE,{"disambiguationData":[OSD([sQuery(id+"F4.wireOp",EDGE,"E30")])]}),makeQuery(id+"F8.opExtrude","SWEPT_FACE",FACE,{"disambiguationData":[OSD([sQuery(id+"F7.wireOp",EDGE,"E67")])]})]});
            fillet(context, id + "F14", {"entities" : qUnion([Q0, Q1, Q2, Q3, Q4, Q5]), "radius" : 3 * mm, "tangentPropagation" : true, "allowEdgeOverflow" : false});
        }
        {
            var Q0;
            Q0=makeQuery(id+"F1.opExtrude","CAP_EDGE",EDGE,{"disambiguationData":[OSD([sQuery(id+"F0.wireOp",EDGE,"E1.bottom")])],"isStart":false});
            fillet(context, id + "F15", {"entities" : qUnion([Q0]), "radius" : 2 * mm, "tangentPropagation" : true, "allowEdgeOverflow" : false});
        }
        {
            var Q0;
            {var subQ0=sQuery(id+"F0.wireOp",EDGE,"E21.filletArc");var subQ1=sQuery(id+"F0.wireOp",EDGE,"E7");var subQ2=sQuery(id+"F0.wireOp",EDGE,"E6");var subQ3=sQuery(id+"F0.wireOp",EDGE,"E5");var subQ4=sQuery(id+"F0.wireOp",EDGE,"E4");var subQ5=sQuery(id+"F0.wireOp",EDGE,"E22.filletArc");var subQ6=sQuery(id+"F0.wireOp",EDGE,"E1.bottom");var subQ7=sQuery(id+"F0.wireOp",EDGE,"E1.right");var subQ8=sQuery(id+"F0.wireOp",EDGE,"E1.top");var subQ9=sQuery(id+"F0.wireOp",EDGE,"E1.left");var subQ10=sQuery(id+"F0.wireOp",EDGE,"E23.filletArc");var subQ11=sQuery(id+"F0.wireOp",EDGE,"E24.filletArc");Q0=makeQuery(id+"F2.boolean.opBoolean","SPLIT",FACE,{"disambiguationData":[TD([makeQuery(id+"F1.opExtrude","SWEPT_FACE",FACE,{"disambiguationData":[OSD([subQ6])]})])],"derivedFrom":makeQuery(id+"F1.opExtrude","CAP_FACE",FACE,{"disambiguationData":[OSD([subQ6,subQ8,subQ9,subQ7,subQ4,subQ3,subQ2,subQ1,subQ0,subQ5,subQ10,subQ11])],"isStart":true})});}
            var sketch = newSketch(context, id + "F16", { "sketchPlane" : qUnion([Q0])});
            skCircle(sketch, "E79", {"center": v(0, 120) * mm, "radius": 6 * mm});
            skPoint(sketch, "E79.centerSnap0", {"position": v(0, 90) * mm});
            skLineSegment(sketch, "E80", {"start": v(0, 90) * mm, "end": v(0, 120) * mm, "construction": true});
            skArc(sketch, "E81", {"start": v(15, 120) * mm, "mid": v(0, 135) * mm, "end": v(-15, 120) * mm});
            skLineSegment(sketch, "E82", {"start": v(-15, 120) * mm, "end": v(-15, 108) * mm});
            skLineSegment(sketch, "E83", {"start": v(-15, 108) * mm, "end": v(-33, 90) * mm});
            skLineSegment(sketch, "E84", {"start": v(15, 120) * mm, "end": v(15, 108) * mm});
            skLineSegment(sketch, "E85", {"start": v(15, 108) * mm, "end": v(33, 90) * mm});
            skLineSegment(sketch, "E86", {"start": v(-80, 0) * mm, "end": v(80, 0) * mm, "construction": true});
            skCircle(sketch, "E87.MirrorC", {"center": v(0, -120) * mm, "radius": 6 * mm});
            skLineSegment(sketch, "E88.MirrorCS", {"start": v(15, -108) * mm, "end": v(33, -90) * mm});
            skLineSegment(sketch, "E89.MirrorCS", {"start": v(15, -120) * mm, "end": v(15, -108) * mm});
            skLineSegment(sketch, "E90.MirrorCS", {"start": v(-15, -108) * mm, "end": v(-33, -90) * mm});
            skLineSegment(sketch, "E91.MirrorCS", {"start": v(-15, -120) * mm, "end": v(-15, -108) * mm});
            skArc(sketch, "E92.MirrorCS", {"start": v(15, -120) * mm, "mid": v(0, -135) * mm, "end": v(-15, -120) * mm});
            skPoint(sketch, "E93.MirrorP", {"position": v(0, -90) * mm});
            skLineSegment(sketch, "E94.MirrorCS", {"start": v(0, -90) * mm, "end": v(0, -120) * mm, "construction": true});
            skSolve(sketch);
        }
        {
            var Q0;
            Q0=makeQuery(id+"F16.imprint","IMPRINT",FACE,{"disambiguationData":[TD([[makeQuery(id+"F16.imprint","IMPRINT",EDGE,{"derivedFrom":sQuery(id+"F16.wireOp",EDGE,"E87.MirrorC")}),1.0]])]});
            var Q1;
            Q1=makeQuery(id+"F16.imprint","IMPRINT",FACE,{"disambiguationData":[TD([[makeQuery(id+"F16.imprint","IMPRINT",EDGE,{"derivedFrom":sQuery(id+"F16.wireOp",EDGE,"E79")}),-1.0]])]});
            var Q2;
            Q2=makeQuery(id+"F16.imprint","IMPRINT",FACE,{"disambiguationData":[TD([[makeQuery(id+"F16.imprint","IMPRINT",EDGE,{"derivedFrom":makeQuery(id+"F1.opExtrude","CAP_EDGE",EDGE,{"disambiguationData":[OSD([sQuery(id+"F0.wireOp",EDGE,"E1.left")])],"isStart":true})}),-1.0]])]});
            var Q3;
            Q3=makeQuery(id+"F2.opExtrude","CAP_FACE",FACE,{"disambiguationData":[OSD([sQuery(id+"F0.wireOp",EDGE,"E12"),sQuery(id+"F0.wireOp",EDGE,"E13"),sQuery(id+"F0.wireOp",EDGE,"E14"),sQuery(id+"F0.wireOp",EDGE,"E15"),sQuery(id+"F0.wireOp",EDGE,"E17.filletArc"),sQuery(id+"F0.wireOp",EDGE,"E18.filletArc"),sQuery(id+"F0.wireOp",EDGE,"E19.filletArc"),sQuery(id+"F0.wireOp",EDGE,"E20.filletArc"),sQuery(id+"F0.wireOp",EDGE,"E25.0"),sQuery(id+"F0.wireOp",EDGE,"E25.1"),sQuery(id+"F0.wireOp",EDGE,"E25.2"),sQuery(id+"F0.wireOp",EDGE,"E25.3"),sQuery(id+"F0.wireOp",EDGE,"E25.4"),sQuery(id+"F0.wireOp",EDGE,"E25.5"),sQuery(id+"F0.wireOp",EDGE,"E25.6"),sQuery(id+"F0.wireOp",EDGE,"E25.7")])],"isStart":false});
            extrude(context, id + "F17", {"entities" : qUnion([Q0, Q1, Q2]), "operationType" : NewBodyOperationType.ADD, "endBound" : BoundingType.UP_TO_SURFACE, "endBoundEntityFace" : qUnion([Q3]), "depth" : 25.4 * mm});
        }
    });
